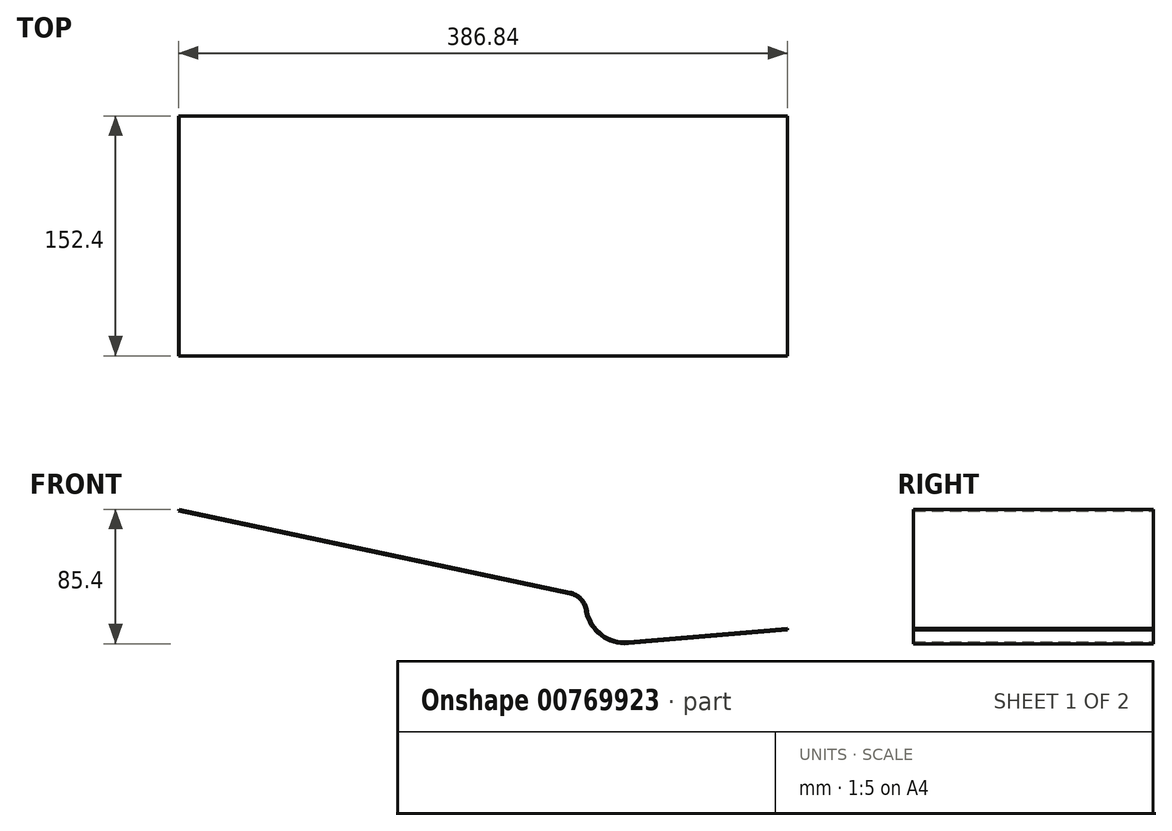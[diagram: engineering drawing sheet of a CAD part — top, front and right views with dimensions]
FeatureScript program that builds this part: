
annotation { "Feature Type Name" : "Feature", "Feature Type Description" : "" }
export const myFeature = defineFeature(function(context is Context, id is Id, definition is map)
    precondition{}
    {
        {
            var Q0;
            Q0=qCreatedBy(makeId("Front.planeOp"),FACE);
            var sketch = newSketch(context, id + "F0", { "sketchPlane" : qUnion([Q0])});
            skLineSegment(sketch, "E0", {"start": v(-586.85, 238.6) * mm, "end": v(-338.38, 185.88) * mm});
            skLineSegment(sketch, "E1", {"start": v(-328.56, 175.95) * mm, "end": v(-328.3, 174.65) * mm});
            skLineSegment(sketch, "E2", {"start": v(-301.24, 154.32) * mm, "end": v(-200, 162.94) * mm});
            skLineSegment(sketch, "E3", {"start": v(-513.01, 152.4) * mm, "end": v(195.3, 152.4) * mm, "construction": true});
            skPoint(sketch, "E4.visualSharp", {"position": v(-330.2, 184.15) * mm});
            skArc(sketch, "E4.filletArc", {"start": v(-328.56, 175.95) * mm, "mid": v(-331.98, 182.39) * mm, "end": v(-338.38, 185.88) * mm});
            skPoint(sketch, "E5.visualSharp", {"position": v(-323.85, 152.4) * mm});
            skArc(sketch, "E5.filletArc", {"start": v(-328.3, 174.65) * mm, "mid": v(-318.65, 159.32) * mm, "end": v(-301.24, 154.32) * mm});
            skLineSegment(sketch, "E6.5", {"start": v(-586.63, 239.63) * mm, "end": v(-338.16, 186.93) * mm});
            skArc(sketch, "E6.6", {"start": v(-327.51, 176.16) * mm, "mid": v(-331.22, 183.14) * mm, "end": v(-338.16, 186.93) * mm});
            skLineSegment(sketch, "E6.7", {"start": v(-327.51, 176.16) * mm, "end": v(-327.25, 174.86) * mm});
            skArc(sketch, "E6.8", {"start": v(-327.25, 174.86) * mm, "mid": v(-318, 160.18) * mm, "end": v(-301.33, 155.39) * mm});
            skLineSegment(sketch, "E6.9", {"start": v(-301.33, 155.39) * mm, "end": v(-200.1, 164) * mm});
            skPoint(sketch, "E7", {"position": v(-200, 162.94) * mm});
            skPoint(sketch, "E8", {"position": v(-586.85, 238.6) * mm});
            skLineSegment(sketch, "E9", {"start": v(-200, 162.94) * mm, "end": v(-200.1, 164) * mm});
            skLineSegment(sketch, "E10", {"start": v(-586.85, 238.6) * mm, "end": v(-586.63, 239.63) * mm});
            skSolve(sketch);
        }
        {
            var Q0;
            Q0 = qSketchRegion(id + "F0", true);
            extrude(context, id + "F1", {"entities" : qUnion([Q0]), "depth" : 152.4 * mm, "offsetDistance" : 25.4 * mm});
        }
    });
